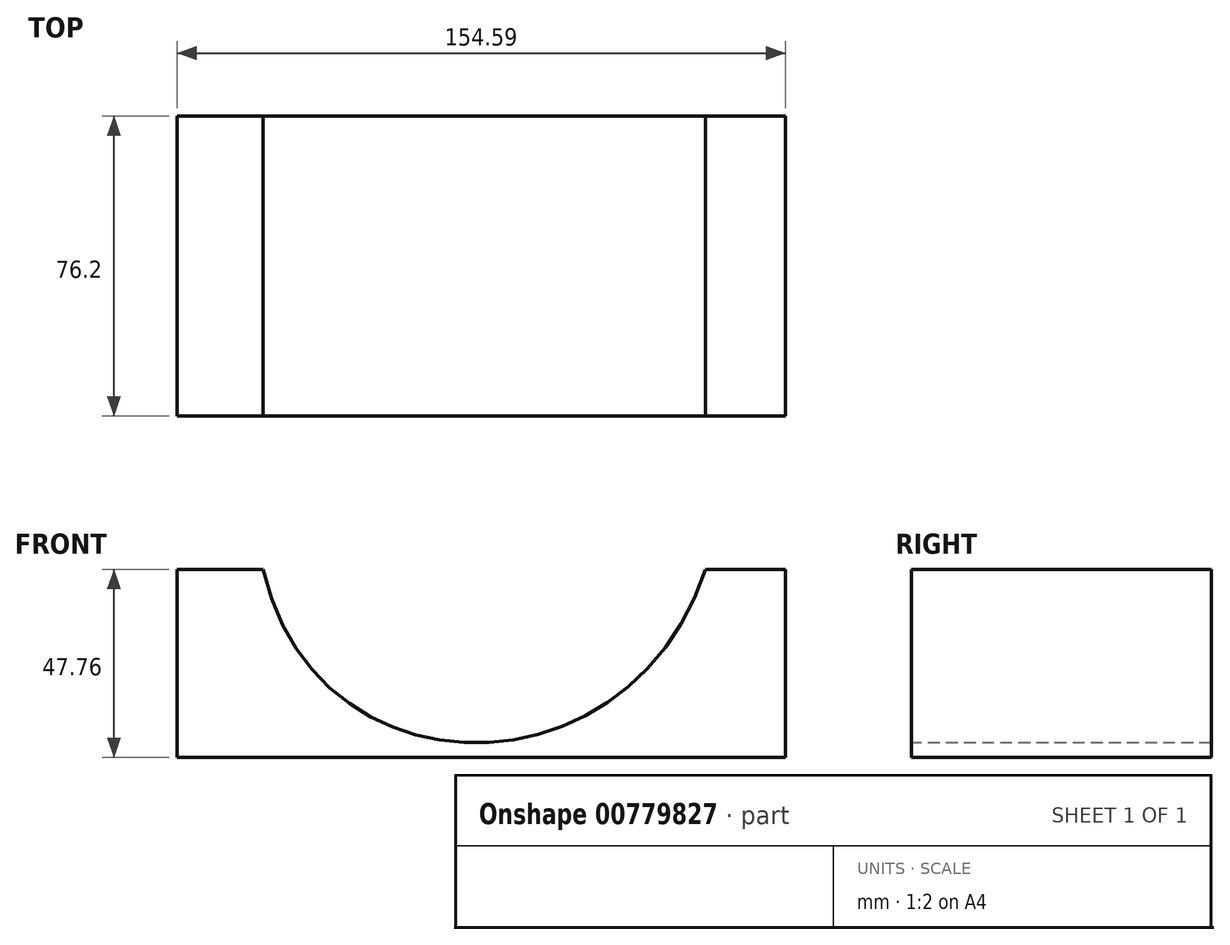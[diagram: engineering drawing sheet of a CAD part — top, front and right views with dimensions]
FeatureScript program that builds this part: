
annotation { "Feature Type Name" : "Feature", "Feature Type Description" : "" }
export const myFeature = defineFeature(function(context is Context, id is Id, definition is map)
    precondition{}
    {
        {
            var Q0;
            Q0=qCreatedBy(makeId("Front.planeOp"),FACE);
            var sketch = newSketch(context, id + "F0", { "sketchPlane" : qUnion([Q0])});
            skLineSegment(sketch, "E0", {"start": v(0, 0) * mm, "end": v(-76.18, 0) * mm});
            skLineSegment(sketch, "E1", {"start": v(-76.18, 0) * mm, "end": v(-76.18, 47.76) * mm});
            skLineSegment(sketch, "E2", {"start": v(-76.18, 47.76) * mm, "end": v(-54.28, 47.76) * mm});
            skLineSegment(sketch, "E3", {"start": v(0, 0) * mm, "end": v(78.68, 0) * mm});
            skLineSegment(sketch, "E4", {"start": v(78.41, 0) * mm, "end": v(78.41, 47.76) * mm});
            skLineSegment(sketch, "E5", {"start": v(78.41, 47.76) * mm, "end": v(58.1, 47.76) * mm});
            skFitSpline(sketch, "E6", {"points": [v(-54.28, 47.76) * mm, v(58.1, 47.76) * mm], "startDerivative": vector(40.54, -177.52) * mm, "endDerivative": vector(56.26, 174.73) * mm});
            skPoint(sketch, "E7", {"position": v(39.34, 0) * mm});
            skSolve(sketch);
        }
        {
            var Q0;
            {var subQ1=sQuery(id+"F0.wireOp",EDGE,"E0");Q0=makeQuery(id+"F0.imprint","IMPRINT",FACE,{"disambiguationData":[TD([[makeQuery(id+"F0.imprint","IMPRINT",EDGE,{"derivedFrom":subQ1}),-1.0]])]});}
            extrude(context, id + "F1", {"entities" : qUnion([Q0]), "oppositeDirection" : true, "depth" : 0.25 * mm, "offsetDistance" : 25.4 * mm, "hasSecondDirection" : true, "secondDirectionOppositeDirection" : false, "secondDirectionDepth" : 75.95 * mm});
        }
    });
